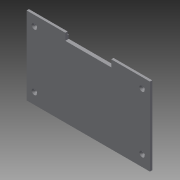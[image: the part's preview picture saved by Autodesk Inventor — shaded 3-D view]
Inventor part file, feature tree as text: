
AUTODESK INVENTOR PART (.ipt)
format: ipt  version: 2015 (Build 190159000, 159)  size: 160,256 bytes
history: native  units: in
note: dims shown in document units (in); Inventor stores cm internally (conversion verified against a paired STEP export)
features: extrude x3, sketch x3, chamfer x1, reference x1
ambient origin geometry x8: Origin, YZ Plane, XZ Plane, XY Plane, X Axis, Y Axis, Z Axis, Center Point
bodies: Solid1 (feature_tree)
feature tree (8):
  extrude  "Extrusion1"  Depth=1.5787in
  extrude  "Extrusion4"  Depth=2.6772in
  extrude  "Extrusion5"  Depth=0.1024in
  chamfer  "Chamfer3"  Distance=0.1024in
  sketch  "Sketch1"  dims[d0=0.1181in d1=0.0in d37=1.5787in]
  sketch  "Sketch4"  dims[d38=4.2362in d39=2.6772in]
  sketch  "Sketch5"  dims[d42=0.1024in d43=0.1024in d44=0.1024in d45=0.1024in d46=0.1024in d48=0.1024in d49=0.2008in d50=0.1024in d51=0.1024in d52=2.4795in d53=0.0394in d54=0.0in d55=0.1102in d56=0.1102in d57=0.1102in d58=0.1102in d59=0.1575in d60=0.0in d61=0.0394in d62=0.0787in d63=45.0deg d64=0.2402in d65=0.0787in]
  reference  "Reference29"
